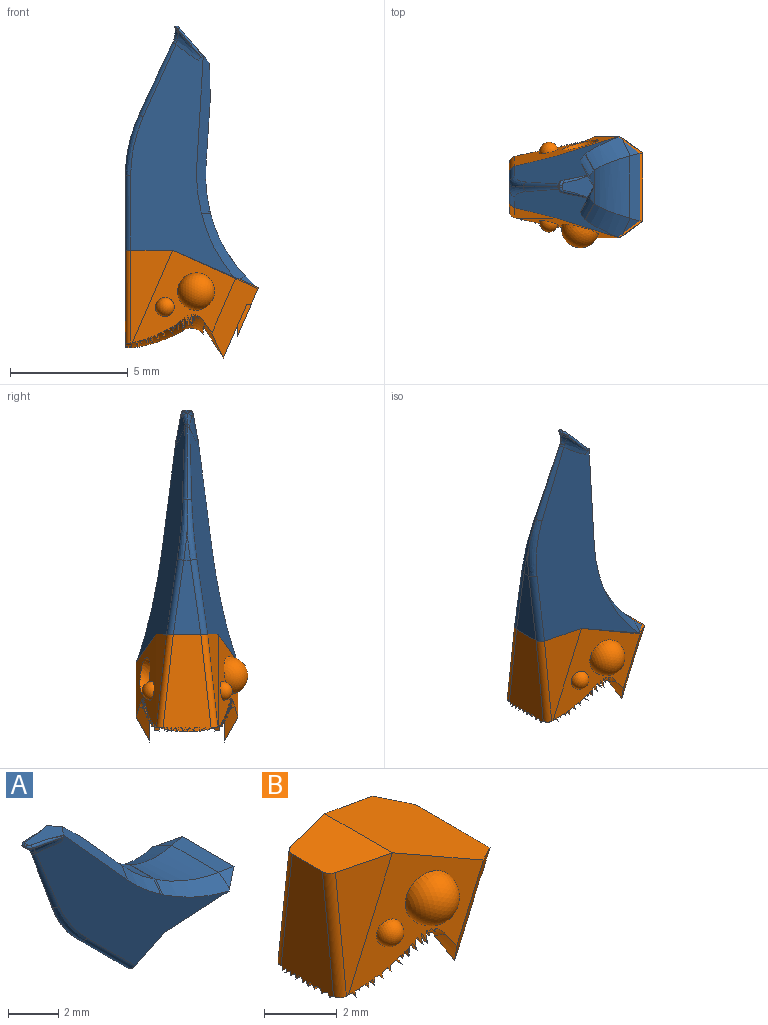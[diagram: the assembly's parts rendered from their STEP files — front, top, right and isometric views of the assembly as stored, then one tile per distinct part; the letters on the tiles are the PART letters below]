
ASSEMBLY  parts=2 mates=1
PART A: 50 faces, bbox 11.1x4.8x8.4 mm
  f0: cylinder r=1.29mm len=0.03mm, axis (0,-1,0), area 0mm2, adj f30,f46,f48
  f1: plane 8.87x8.11mm, normal (-0.27,-0.96,-0.07), area 23.4mm2, adj f9,f10,f12,f14,f15,f16,f17,f23
  f2: plane 8.87x8.11mm, normal (-0.27,0.96,-0.07), area 23.4mm2, adj f9,f10,f12,f18,f19,f20,f21,f26
  f3: cylinder r=6.35mm len=0.95mm, axis (0,-1,0), area 0.2mm2, adj f11,f39,f42
  f4: plane 2.1x1.85mm, normal (0.75,0,0.66), area 1.1mm2, adj f5,f17,f18
  f5: cylinder r=6.35mm len=1.48mm, axis (0,-1,0), area 2.1mm2, adj f4,f6,f16,f19
  f6: plane 1.42x0.09mm, normal (0.52,0,0.86), area 0.1mm2, adj f5,f7,f15,f20
  f7: cylinder r=5.68mm len=2.94mm, axis (0,-1,0), area 6.3mm2, adj f6,f8,f14,f21
  f8: plane 2.91x0.72mm, normal (0,0,1), area 2mm2, adj f7,f9,f13,f22
  f9: plane 4.31x3.72mm, normal (0.35,0,-0.93), area 13.9mm2, adj f1,f2,f8,f10,f13,f14,f21,f22
  f10: plane 2.64x1.42mm, normal (0.71,0,-0.71), area 4.2mm2, adj f1,f2,f9,f11,f38,f40
  f11: plane 2.21x2.21mm, normal (-0.71,0,-0.71), area 2.3mm2, adj f3,f10,f38,f40
  f12: plane 2.03x0.93mm, normal (0.08,0,1), area 1.1mm2, adj f1,f2,f17,f18,f33,f34,f35,f36
  f13: plane 0.86x0.75mm, normal (-0.07,-0.39,0.92), area 0.3mm2, adj f8,f9,f14
  f14: bspline ~3.38x1.66mm, area 2.8mm2, adj f1,f7,f9,f13,f15
  f15: plane 0.7x0.38mm, normal (0.39,-0.46,0.8), area 0.1mm2, adj f1,f6,f14,f16
  f16: bspline ~2.04x1.63mm, area 1.6mm2, adj f1,f5,f15,f17
  f17: plane 3.42x3.39mm, normal (0.61,-0.5,0.62), area 3.4mm2, adj f1,f4,f12,f16,f18
  f18: plane 3.42x3.39mm, normal (0.61,0.5,0.62), area 3.4mm2, adj f2,f4,f12,f17,f19
  f19: bspline ~2.04x1.63mm, area 1.6mm2, adj f2,f5,f18,f20
  f20: plane 0.7x0.38mm, normal (0.39,0.46,0.8), area 0.1mm2, adj f2,f6,f19,f21
  f21: bspline ~3.38x1.66mm, area 2.8mm2, adj f2,f7,f9,f20,f22
  f22: plane 0.86x0.75mm, normal (-0.07,0.39,0.92), area 0.3mm2, adj f8,f9,f21
  f23: plane 0.25x0.07mm, normal (1,0,-0.08), area 0mm2, adj f1,f25,f28,f33
  f24: plane 0.11x0.03mm, normal (-1,0,0.08), area 0mm2, adj f30,f31,f32,f37
  f25: plane 1.54x0.21mm, normal (-0.13,-0.99,0.01), area 0mm2, adj f23,f28,f31,f33,f43
  f26: plane 0.25x0.06mm, normal (1,0,-0.08), area 0mm2, adj f2,f27,f29,f34
  f27: plane 1.54x0.21mm, normal (-0.13,0.99,0.01), area 0mm2, adj f26,f29,f32,f34,f49
  f28: bspline ~2.52x0.7mm, area 0.5mm2, adj f1,f23,f25,f43,f44,f46
  f29: bspline ~2.17x0.6mm, area 0.5mm2, adj f2,f26,f27,f47,f48,f49
  f30: cylinder r=0.13mm len=0.28mm, axis (0,-1,0), area 0mm2, adj f0,f24,f31,f32,f43,f49
  f31: cylinder r=0.2mm len=0.2mm, axis (-0.08,0,-1), area 0mm2, adj f24,f25,f30,f35,f43
  f32: cylinder r=0.2mm len=0.2mm, axis (0.08,0,1), area 0mm2, adj f24,f27,f30,f36,f49
  f33: cylinder r=0.09mm len=1.56mm, axis (-0.99,0.13,0.07), area 0.2mm2, adj f1,f12,f23,f25,f35
  f34: cylinder r=0.09mm len=1.56mm, axis (0.99,0.13,-0.07), area 0.2mm2, adj f2,f12,f26,f27,f36
  f35: torus R=0.11mm, axis (-0.08,0,-1), area 0mm2, adj f12,f31,f33,f37
  f36: torus R=0.11mm, axis (-0.08,0,-1), area 0mm2, adj f12,f32,f34,f37
  f37: cylinder r=0.09mm len=0.11mm, axis (0,1,0), area 0mm2, adj f12,f24,f35,f36
  f38: cylinder r=0.29mm len=2.43mm, axis (0.7,-0.14,-0.7), area 1.2mm2, adj f1,f10,f11,f39
  f39: bspline ~3.34x2.05mm, area 0.9mm2, adj f1,f3,f38,f41,f42
  f40: cylinder r=0.29mm len=2.43mm, axis (-0.7,-0.14,0.7), area 1.2mm2, adj f2,f10,f11,f42
  f41: cylinder r=0.29mm len=3.24mm, axis (-0.35,0.03,0.93), area 0.8mm2, adj f1,f39,f44,f45
  f42: bspline ~3.09x1.98mm, area 0.9mm2, adj f2,f3,f39,f40,f45
  f43: bspline ~0.3x0.28mm, area 0mm2, adj f25,f28,f30,f31,f46
  f44: bspline ~0.44x0.35mm, area 0mm2, adj f28,f41,f46,f47
  f45: cylinder r=0.29mm len=3.24mm, axis (0.35,0.03,-0.93), area 0.8mm2, adj f2,f41,f42,f47
  f46: bspline ~0.32x0.3mm, area 0mm2, adj f0,f28,f43,f44,f47,f48
  f47: bspline ~0.29x0.29mm, area 0mm2, adj f29,f44,f45,f46,f48
  f48: bspline ~0.54x0.53mm, area 0.1mm2, adj f0,f29,f46,f47,f49
  f49: bspline ~0.3x0.28mm, area 0mm2, adj f27,f29,f30,f32,f48
PART B: 156 faces, bbox 5.7x5.4x4.7 mm
  f0: plane 0.06x0.06mm, normal (1,0,0), area 0mm2, adj f1,f152,f153,f154,f155
  f1: plane 0.25x0.01mm, normal (0,1,0.06), area 0mm2, adj f0,f2,f152,f155
  f2: plane 4.14x2.03mm, normal (-1,0,0), area 6.5mm2, adj f1,f3,f6,f8,f10,f11,f12,f13
  f3: plane 0.25x0.13mm, normal (0,0.84,-0.55), area 0mm2, adj f2,f4,f5,f6,f151
  f4: plane 0.06x0.06mm, normal (1,0,0), area 0mm2, adj f3,f151,f153
  f5: plane 0.26x0.13mm, normal (-1,0,0), area 0mm2, adj f3,f6,f153
  f6: cylinder r=0.43mm len=0.25mm, axis (-1,0,0), area 0.1mm2, adj f2,f3,f5,f7,f8
  f7: plane 0.03x0.02mm, normal (1,0,0), area 0mm2, adj f6,f8,f153
  f8: plane 0.25x0.15mm, normal (0,0.94,-0.35), area 0mm2, adj f2,f6,f7,f9,f10
  f9: plane 0.99x0.17mm, normal (-1,0,0), area 0.1mm2, adj f8,f10,f11,f12,f13,f14,f15,f16
  f10: plane 0.25x0.16mm, normal (0,0,-1), area 0mm2, adj f2,f8,f9,f11
  f11: cylinder r=0.08mm len=0.25mm, axis (-1,0,0), area 0mm2, adj f2,f9,f10,f12
  f12: cylinder r=0.5mm len=0.25mm, axis (-1,0,0), area 0.1mm2, adj f2,f9,f11,f13
  f13: cylinder r=0.14mm len=0.25mm, axis (-1,0,0), area 0.1mm2, adj f2,f9,f12,f14
  f14: plane 0.25x0.16mm, normal (0,0.86,-0.51), area 0mm2, adj f2,f9,f13,f15
  f15: plane 0.25x0.15mm, normal (0,-0.79,-0.61), area 0mm2, adj f2,f9,f14,f16
  f16: cylinder r=0.15mm len=0.25mm, axis (-1,0,0), area 0mm2, adj f2,f9,f15,f17
  f17: plane 0.25x0.11mm, normal (0,0,-1), area 0mm2, adj f2,f9,f16,f18
  f18: plane 0.25x0.15mm, normal (0,-0.85,-0.52), area 0mm2, adj f2,f9,f17,f19,f20
  f19: plane 0.01x0mm, normal (1,0,0), area 0mm2, adj f18,f20,f153
  f20: cylinder r=0.15mm len=0.25mm, axis (-1,0,0), area 0mm2, adj f2,f18,f19,f21,f22
  f21: plane 0.19x0.14mm, normal (-1,0,0), area 0mm2, adj f20,f22,f153
  f22: plane 0.25x0.17mm, normal (0,-0.67,-0.75), area 0.1mm2, adj f2,f20,f21,f23,f24
  f23: plane 0.04x0.04mm, normal (1,0,0), area 0mm2, adj f22,f24,f153
  f24: cylinder r=0.15mm len=0.25mm, axis (-1,0,0), area 0mm2, adj f2,f22,f23,f25,f26
  f25: plane 0.14x0.12mm, normal (-1,0,0), area 0mm2, adj f24,f26,f153
  f26: plane 0.25x0.21mm, normal (0,-0.61,-0.79), area 0.1mm2, adj f2,f24,f25,f27,f28
  f27: plane 0.09x0.07mm, normal (1,0,0), area 0mm2, adj f26,f28,f153
  f28: cylinder r=0.16mm len=0.25mm, axis (-1,0,0), area 0mm2, adj f2,f26,f27,f29,f30
  f29: plane 0.1x0.09mm, normal (-1,0,0), area 0mm2, adj f28,f30,f152,f153
  f30: plane 0.25x0.04mm, normal (0,0,-1), area 0mm2, adj f2,f28,f29,f152
  f31: plane 0.25x0.07mm, normal (0,0,-1), area 0mm2, adj f2,f32,f34,f154
  f32: plane 0.22x0.06mm, normal (-1,0,0), area 0mm2, adj f31,f33,f34,f153,f154
  f33: plane 0.27x0.22mm, normal (0,0,-1), area 0mm2, adj f32,f34,f35,f153
  f34: plane 0.25x0.01mm, normal (0,1,0), area 0mm2, adj f31,f32,f33
  f35: cylinder r=0.29mm len=4.03mm, axis (0,-0.11,0.99), area 1.5mm2, adj f2,f33,f36,f146,f153
  f36: plane 3.94x1.77mm, normal (-0.24,0.96,0.1), area 3.7mm2, adj f35,f37,f146,f153
  f37: plane 4.4x4.09mm, normal (-0.25,0.96,0.11), area 6.6mm2, adj f36,f38,f39,f40,f102,f103,f105,f106
  f38: sphere r=0.79mm, area 4mm2, adj f37
  f39: sphere r=0.4mm, area 1mm2, adj f37
  f40: plane 3.49x2.06mm, normal (0.51,0.83,-0.22), area 3.3mm2, adj f37,f41,f98,f101,f102,f145
  f41: plane 2.91x2.07mm, normal (0.92,0,-0.4), area 5.4mm2, adj f40,f42,f94,f95,f96,f97,f101,f102
  f42: plane 3.49x2.06mm, normal (0.51,-0.83,-0.22), area 3.3mm2, adj f41,f43,f44,f89,f97,f102
  f43: cone r=3.67mm half-angle=55.5deg, axis (1,0,0), area 0.6mm2, adj f42,f44,f89,f144
  f44: plane 4.4x4.09mm, normal (-0.25,-0.96,0.11), area 6.6mm2, adj f42,f43,f45,f46,f47,f49,f51,f52
  f45: sphere r=0.79mm, area 4mm2, adj f44
  f46: sphere r=0.4mm, area 1mm2, adj f44
  f47: plane 0.28x0.24mm, normal (-0.97,0.25,-0.03), area 0.1mm2, adj f44,f48,f88,f153
  f48: plane 0.23x0.04mm, normal (0.25,0.96,-0.11), area 0mm2, adj f47,f88,f153
  f49: plane 0.22x0.21mm, normal (0.85,-0.28,-0.45), area 0mm2, adj f44,f50,f51,f153
  f50: plane 0.12x0.06mm, normal (0.25,0.96,-0.11), area 0mm2, adj f49,f51,f153
  f51: cylinder r=0.61mm len=0.23mm, axis (-0.25,-0.96,0.11), area 0mm2, adj f44,f49,f50,f153
  f52: cylinder r=1.57mm len=0.28mm, axis (-0.25,-0.96,0.11), area 0.1mm2, adj f44,f53,f54,f153
  f53: plane 0.19x0.17mm, normal (0.25,0.96,-0.11), area 0mm2, adj f52,f54,f153
  f54: plane 0.28x0.26mm, normal (-0.68,0.1,-0.73), area 0.1mm2, adj f44,f52,f53,f153
  f55: cylinder r=0.66mm len=0.24mm, axis (-0.25,-0.96,0.11), area 0mm2, adj f44,f56,f57,f153
  f56: plane 0.15x0.07mm, normal (0.25,0.96,-0.11), area 0mm2, adj f55,f57,f153
  f57: plane 0.25x0.18mm, normal (-0.82,0.15,-0.55), area 0mm2, adj f44,f55,f56,f153
  f58: cylinder r=0.45mm len=0.24mm, axis (-0.25,-0.96,0.11), area 0mm2, adj f44,f59,f60,f153
  f59: plane 0.16x0.11mm, normal (0.25,0.96,-0.11), area 0mm2, adj f58,f60,f153
  f60: plane 0.26x0.19mm, normal (-0.7,0.11,-0.7), area 0mm2, adj f44,f58,f59,f153
  f61: cylinder r=1.1mm len=0.25mm, axis (-0.25,-0.96,0.11), area 0mm2, adj f44,f62,f63,f153
  f62: plane 0.19x0.06mm, normal (0.25,0.96,-0.11), area 0mm2, adj f61,f63,f153
  f63: plane 0.24x0.22mm, normal (-0.94,0.22,-0.27), area 0mm2, adj f44,f61,f62,f153
  f64: cylinder r=0.59mm len=0.22mm, axis (-0.25,-0.96,0.11), area 0mm2, adj f44,f65,f66,f153
  f65: plane 0.13x0.07mm, normal (0.25,0.96,-0.11), area 0mm2, adj f64,f66,f153
  f66: plane 0.24x0.16mm, normal (-0.89,0.19,-0.41), area 0mm2, adj f44,f64,f65,f153
  f67: cylinder r=0.6mm len=0.22mm, axis (-0.25,-0.96,0.11), area 0mm2, adj f44,f68,f69,f153
  f68: plane 0.04x0.02mm, normal (0.25,0.96,-0.11), area 0mm2, adj f67,f69,f153
  f69: plane 0.22x0.09mm, normal (-0.85,0.17,-0.49), area 0mm2, adj f44,f67,f68,f153
  f70: cylinder r=0.61mm len=0.24mm, axis (-0.25,-0.96,0.11), area 0mm2, adj f44,f71,f72,f153
  f71: plane 0.18x0.09mm, normal (0.25,0.96,-0.11), area 0mm2, adj f70,f72,f153
  f72: plane 0.26x0.22mm, normal (-0.84,0.16,-0.51), area 0mm2, adj f44,f70,f71,f153
  f73: plane 3.94x1.77mm, normal (-0.24,-0.96,0.1), area 3.7mm2, adj f44,f146,f147,f153
  f74: cylinder r=0.06mm len=0.16mm, axis (-0.25,-0.96,0.11), area 0mm2, adj f44,f75,f144
  f75: plane 0.16x0.15mm, normal (-0.78,0.13,-0.61), area 0mm2, adj f44,f74,f144
  f76: cylinder r=0.48mm len=0.23mm, axis (-0.25,-0.96,0.11), area 0mm2, adj f44,f77,f78,f144
  f77: plane 0.1x0.03mm, normal (0.25,0.96,-0.11), area 0mm2, adj f76,f78,f144
  f78: plane 0.23x0.23mm, normal (-0.92,0.2,-0.33), area 0mm2, adj f44,f76,f77,f144
  f79: cylinder r=1.01mm len=0.44mm, axis (-0.25,-0.96,0.11), area 0.1mm2, adj f44,f80,f81,f144
  f80: plane 0.31x0.12mm, normal (0.25,0.96,-0.11), area 0mm2, adj f79,f81,f144
  f81: plane 0.4x0.28mm, normal (-0.9,0.19,-0.4), area 0.1mm2, adj f44,f79,f80,f144
  f82: cylinder r=0.72mm len=0.39mm, axis (-0.25,-0.96,0.11), area 0.1mm2, adj f44,f83,f84,f144
  f83: plane 0.27x0.12mm, normal (0.25,0.96,-0.11), area 0mm2, adj f82,f84,f144
  f84: plane 0.31x0.27mm, normal (-0.85,0.17,-0.5), area 0.1mm2, adj f44,f82,f83,f144
  f85: cylinder r=1.24mm len=0.37mm, axis (-0.25,-0.96,0.11), area 0.1mm2, adj f44,f86,f87,f144
  f86: plane 0.29x0.09mm, normal (0.25,0.96,-0.11), area 0mm2, adj f85,f87,f144
  f87: plane 0.3x0.26mm, normal (-0.9,0.19,-0.38), area 0.1mm2, adj f44,f85,f86,f144,f153
  f88: cylinder r=1.86mm len=0.32mm, axis (-0.25,-0.96,0.11), area 0.1mm2, adj f44,f47,f48,f153
  f89: plane 3.07x1.91mm, normal (0,1,0), area 3mm2, adj f42,f43,f90,f91,f92,f97,f144
  f90: cylinder r=0.72mm len=3.14mm, axis (0,-1,0), area 7.1mm2, adj f89,f91,f95,f97,f98,f101
  f91: plane 3.14x1.29mm, normal (1,0,0), area 3.7mm2, adj f89,f90,f98,f144
  f92: cylinder r=0.32mm len=0.64mm, axis (0,1,0), area 0.5mm2, adj f89,f93
  f93: plane 0.64x0.64mm, normal (0,1,0), area 0.3mm2, adj f92
  f94: plane 1.37x0.6mm, normal (0,1,0), area 0.4mm2, adj f41,f95,f101
  f95: plane 2.13x1.37mm, normal (-1,0,0), area 2.9mm2, adj f41,f90,f94,f96
  f96: plane 1.37x0.6mm, normal (0,-1,0), area 0.4mm2, adj f41,f95,f97
  f97: plane 0.6x0.51mm, normal (0,0,-1), area 0.3mm2, adj f41,f42,f89,f90,f96
  f98: plane 3.07x1.91mm, normal (0,-1,0), area 3mm2, adj f40,f90,f91,f99,f101,f144,f145
  f99: cylinder r=0.32mm len=0.64mm, axis (0,-1,0), area 0.5mm2, adj f98,f100
  f100: plane 0.64x0.64mm, normal (0,-1,0), area 0.3mm2, adj f99
  f101: plane 0.6x0.51mm, normal (0,0,-1), area 0.3mm2, adj f40,f41,f90,f94,f98
  f102: plane 4.31x3.65mm, normal (0.4,0,0.92), area 13.9mm2, adj f37,f40,f41,f42,f44,f146
  f103: plane 0.26x0.22mm, normal (-0.84,-0.16,-0.51), area 0mm2, adj f37,f104,f105,f153
  f104: plane 0.18x0.09mm, normal (0.25,-0.96,-0.11), area 0mm2, adj f103,f105,f153
  f105: cylinder r=0.61mm len=0.24mm, axis (-0.25,0.96,0.11), area 0mm2, adj f37,f103,f104,f153
  f106: plane 0.22x0.09mm, normal (-0.85,-0.17,-0.49), area 0mm2, adj f37,f107,f108,f153
  f107: plane 0.04x0.02mm, normal (0.25,-0.96,-0.11), area 0mm2, adj f106,f108,f153
  f108: cylinder r=0.6mm len=0.22mm, axis (-0.25,0.96,0.11), area 0mm2, adj f37,f106,f107,f153
  f109: plane 0.24x0.16mm, normal (-0.89,-0.19,-0.41), area 0mm2, adj f37,f110,f111,f153
  f110: plane 0.13x0.07mm, normal (0.25,-0.96,-0.11), area 0mm2, adj f109,f111,f153
  f111: cylinder r=0.59mm len=0.22mm, axis (-0.25,0.96,0.11), area 0mm2, adj f37,f109,f110,f153
  f112: plane 0.24x0.22mm, normal (-0.94,-0.22,-0.27), area 0mm2, adj f37,f113,f114,f153
  f113: plane 0.19x0.06mm, normal (0.25,-0.96,-0.11), area 0mm2, adj f112,f114,f153
  f114: cylinder r=1.1mm len=0.25mm, axis (-0.25,0.96,0.11), area 0mm2, adj f37,f112,f113,f153
  f115: plane 0.26x0.19mm, normal (-0.7,-0.11,-0.7), area 0mm2, adj f37,f116,f117,f153
  f116: plane 0.16x0.11mm, normal (0.25,-0.96,-0.11), area 0mm2, adj f115,f117,f153
  f117: cylinder r=0.45mm len=0.24mm, axis (-0.25,0.96,0.11), area 0mm2, adj f37,f115,f116,f153
  f118: plane 0.25x0.18mm, normal (-0.82,-0.15,-0.55), area 0mm2, adj f37,f119,f120,f153
  f119: plane 0.15x0.07mm, normal (0.25,-0.96,-0.11), area 0mm2, adj f118,f120,f153
  f120: cylinder r=0.66mm len=0.24mm, axis (-0.25,0.96,0.11), area 0mm2, adj f37,f118,f119,f153
  f121: plane 0.28x0.26mm, normal (-0.68,-0.1,-0.73), area 0.1mm2, adj f37,f122,f123,f153
  f122: plane 0.19x0.17mm, normal (0.25,-0.96,-0.11), area 0mm2, adj f121,f123,f153
  f123: cylinder r=1.57mm len=0.28mm, axis (-0.25,0.96,0.11), area 0.1mm2, adj f37,f121,f122,f153
  f124: cylinder r=0.61mm len=0.23mm, axis (-0.25,0.96,0.11), area 0mm2, adj f37,f125,f126,f153
  f125: plane 0.12x0.06mm, normal (0.25,-0.96,-0.11), area 0mm2, adj f124,f126,f153
  f126: plane 0.22x0.21mm, normal (0.85,0.28,-0.45), area 0mm2, adj f37,f124,f125,f153
  f127: plane 0.28x0.24mm, normal (-0.97,-0.25,-0.03), area 0.1mm2, adj f37,f128,f129,f153
  f128: plane 0.23x0.04mm, normal (0.25,-0.96,-0.11), area 0mm2, adj f127,f129,f153
  f129: cylinder r=1.86mm len=0.32mm, axis (-0.25,0.96,0.11), area 0.1mm2, adj f37,f127,f128,f153
  f130: plane 0.3x0.26mm, normal (-0.9,-0.19,-0.38), area 0.1mm2, adj f37,f131,f132,f144,f153
  f131: plane 0.29x0.09mm, normal (0.25,-0.96,-0.11), area 0mm2, adj f130,f132,f144
  f132: cylinder r=1.24mm len=0.37mm, axis (-0.25,0.96,0.11), area 0.1mm2, adj f37,f130,f131,f144
  f133: plane 0.31x0.27mm, normal (-0.85,-0.17,-0.5), area 0.1mm2, adj f37,f134,f135,f144
  f134: plane 0.27x0.12mm, normal (0.25,-0.96,-0.11), area 0mm2, adj f133,f135,f144
  f135: cylinder r=0.72mm len=0.39mm, axis (-0.25,0.96,0.11), area 0.1mm2, adj f37,f133,f134,f144
  f136: plane 0.4x0.28mm, normal (-0.9,-0.19,-0.4), area 0.1mm2, adj f37,f137,f138,f144
  f137: plane 0.31x0.12mm, normal (0.25,-0.96,-0.11), area 0mm2, adj f136,f138,f144
  f138: cylinder r=1.01mm len=0.44mm, axis (-0.25,0.96,0.11), area 0.1mm2, adj f37,f136,f137,f144
  f139: plane 0.23x0.23mm, normal (-0.92,-0.2,-0.33), area 0mm2, adj f37,f140,f141,f144
  f140: plane 0.1x0.03mm, normal (0.25,-0.96,-0.11), area 0mm2, adj f139,f141,f144
  f141: cylinder r=0.48mm len=0.23mm, axis (-0.25,0.96,0.11), area 0mm2, adj f37,f139,f140,f144
  f142: plane 0.16x0.15mm, normal (-0.78,-0.13,-0.61), area 0mm2, adj f37,f143,f144
  f143: cylinder r=0.06mm len=0.16mm, axis (-0.25,0.96,0.11), area 0mm2, adj f37,f142,f144
  f144: torus R=3.93mm, axis (1,0,0), area 4mm2, adj f37,f43,f44,f74,f75,f76,f77,f78
  f145: cone r=3.67mm half-angle=55.5deg, axis (1,0,0), area 0.6mm2, adj f37,f40,f98,f144
  f146: plane 2.63x2mm, normal (0,0,1), area 4.2mm2, adj f2,f35,f36,f73,f102,f147
  f147: cylinder r=0.29mm len=4.03mm, axis (0,0.11,0.99), area 1.5mm2, adj f2,f73,f146,f148,f153
  f148: plane 0.27x0.22mm, normal (0,0,-1), area 0mm2, adj f147,f149,f150,f153
  f149: plane 0.26x0.07mm, normal (-1,0,0), area 0mm2, adj f148,f150,f151,f153
  f150: plane 0.25x0.01mm, normal (0,-1,0), area 0mm2, adj f148,f149,f151
  f151: cylinder r=0.2mm len=0.25mm, axis (-1,0,0), area 0.1mm2, adj f2,f3,f4,f149,f150
  f152: plane 0.25x0.12mm, normal (0,-0.77,-0.64), area 0mm2, adj f0,f1,f2,f29,f30
  f153: revolved ~4.19x2.31mm, area 7mm2, adj f0,f4,f5,f7,f9,f19,f21,f23
  f154: cylinder r=0.31mm len=0.25mm, axis (-1,0,0), area 0mm2, adj f0,f2,f31,f32,f155
  f155: plane 0.25x0.02mm, normal (0,-0.63,-0.78), area 0mm2, adj f0,f1,f2,f154
PLACE A rot(axis=(0,1,0),45deg) t=(-40.73,-49.79,-9.73)mm
PLACE B t=(-29.75,-49.79,-5.24)mm
MATE fastened A.f10 <-> B.f146  axis (0,0,-1) through (-29.75,-49.79,-5.24)mm
